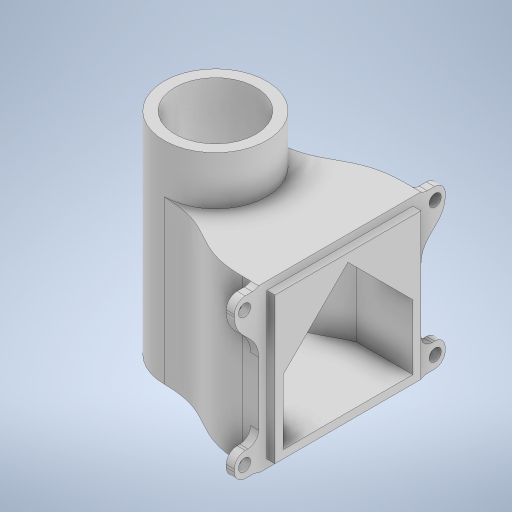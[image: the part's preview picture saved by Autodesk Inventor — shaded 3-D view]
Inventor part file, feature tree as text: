
AUTODESK INVENTOR PART (.ipt)
format: ipt  version: 2024 (Build 280153000, 153)  size: 462,336 bytes
history: native  units: in
note: dims shown in document units (in); Inventor stores cm internally (conversion verified against a paired STEP export)
features: extrude x7, sketch x6, fillet x2, projected_geometry x2, plane x1, hole x1, chamfer x1
ambient origin geometry x8: Origin, YZ Plane, XZ Plane, XY Plane, X Axis, Y Axis, Z Axis, Center Point
bodies: Solid1 (feature_tree)
feature tree (20):
  extrude  "Extrusion1"  Depth=0.0787in
  plane  "Work Plane1"
  extrude  "Extrusion2"  Depth=0.374in
  sketch  "Sketch4"  dims[d5=1.1811in d6=0.1181in]
  extrude  "Extrusion4"  Depth=0.1181in
  hole  "Hole2"  [1 undecoded]
  sketch  "Sketch9"  dims[d10=0.4724in d11=0.1181in]
  extrude  "Extrusion7"  Depth=0.1181in
  extrude  "Extrusion8"  Depth=0.1969in
  extrude  "Extrusion9"  Depth=0.1969in
  extrude  "Extrusion3"  Depth=0.1969in TaperAngle=0.0deg
  fillet  "Fillet1"  Radius=0.0886in
  chamfer  "Chamfer1"  Distance=1.1811in
  fillet  "Fillet2"  Radius=1.1811in
  sketch  "Sketch1"  dims[d0=0.748in d1=0.0787in]
  sketch  "Sketch2"  dims[d2=0.4724in d3=0.0in d4=0.374in]
  projected_geometry  "Projected Loop1"
  sketch  "Sketch8"  dims[d7=0.1181in d9=0.9449in]
  projected_geometry  "Projected Loop5"
  sketch  "Sketch11"  dims[d12=0.1181in d13=1.1811in d20=0.1181in d23=0.5906in d24=0.0in d25=0.0886in d26=1.1811in d27=1.1811in d35=0.0591in d36=0.2362in d37=0.0in d38=0.0591in d39=0.0in d40=0.748in d41=0.0in d53=0.5906in d54=0.1033in d55=0.1033in d56=0.1033in d57=0.1033in d58=0.1033in d60=0.1033in d61=0.1033in d62=0.5906in d63=0.2362in d64=0.1575in d65=0.0787in d66=90.0deg d67=0.3937in d68=0.8108in d69=0.7874in d70=0.0787in d71=0.0787in d72=0.0in d73=0.0in d74=1.1811in d75=0.0in d76=0.1033in d77=0.1033in d78=0.1033in d79=0.1033in d80=0.1772in d82=0.1772in d86=0.0591in d87=0.0in d91=0.0787in d92=0.0148in d93=0.0886in d94=0.1772in d95=0.1772in d99=0.0148in d100=0.1772in d101=0.0787in d102=45.0deg d103=0.1969in d104=0.4724in d105=0.4724in d106=0.4724in]
note: 1 required parameter value undecoded (feature->parameter linkage not recoverable at this tier; creation-order binding heuristic only, values carry confidence <= 0.55)
